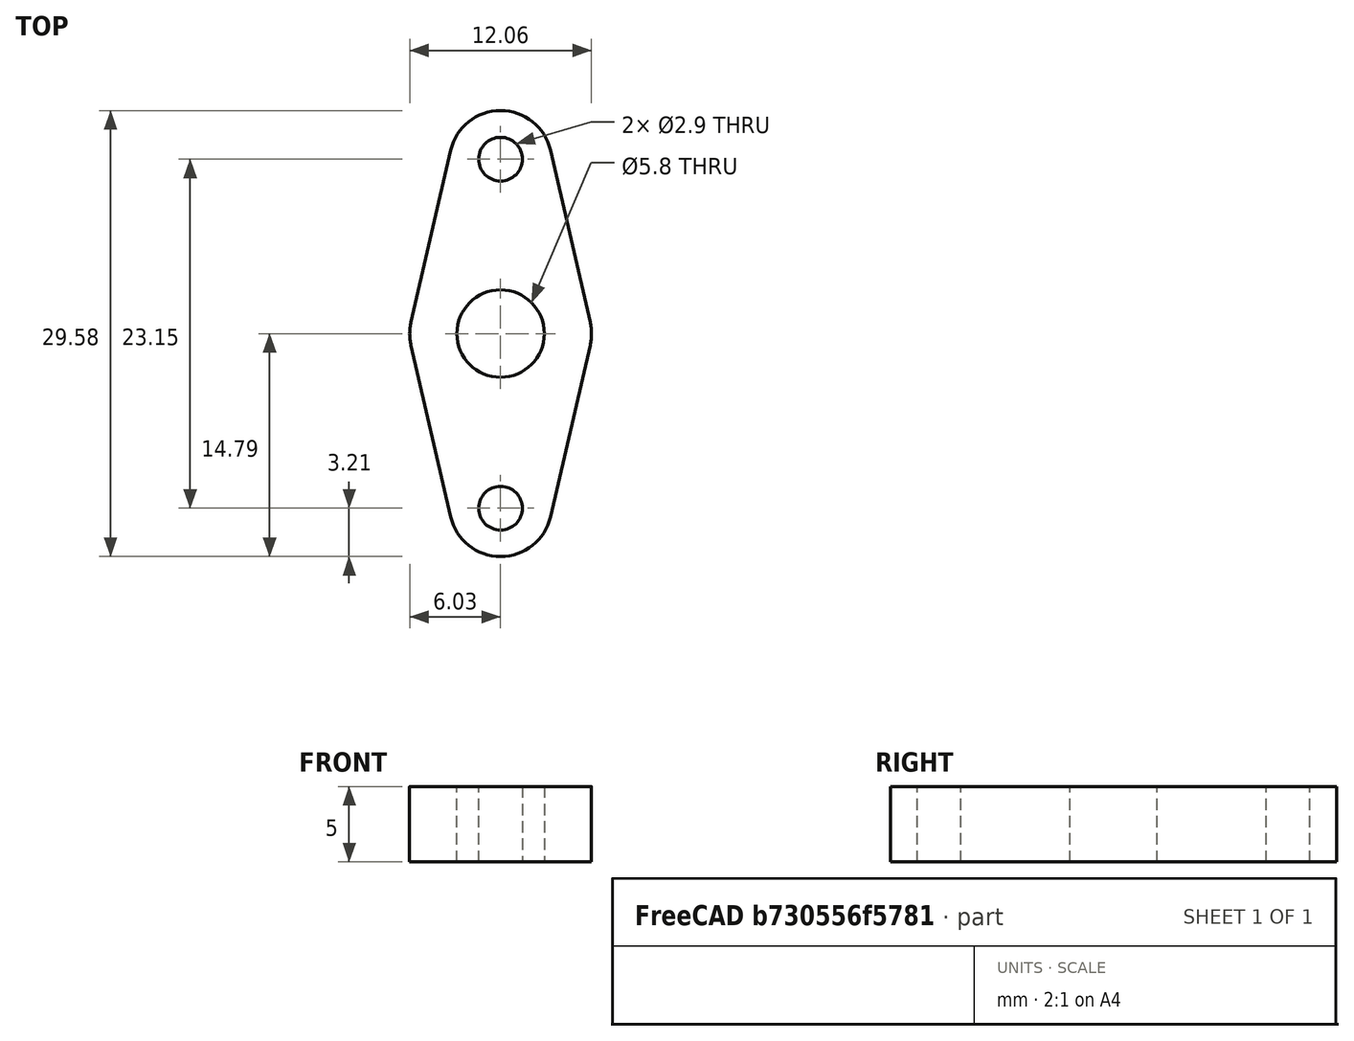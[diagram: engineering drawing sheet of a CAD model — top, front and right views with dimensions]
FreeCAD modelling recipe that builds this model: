
FCSTD DOCUMENT  (FreeCAD 0.21R33771 (Git))
Label: lens_holder_extension
License: All rights reserved
LicenseURL: http://en.wikipedia.org/wiki/All_rights_reserved
objects: Sketcher::SketchObject×2, Mesh::Feature×1, PartDesign::Pad×1, PartDesign::Fillet×1, PartDesign::Pocket×1, PartDesign::Body×1
note: 9 computed .brp shape members not serialized (recipe doc carries the construction recipe); baked Part::Feature solids carry a one-line shape summary decoded from their .brp

FEATURE [Mesh::Feature] EspressoScope_xiao_lensholder_small
  Placement = pos=(-17.04,75.5,10) rot=(0,0,1;0.763582rad)
FEATURE [Sketcher::SketchObject] Sketch
  FullyConstrained = false
  MapMode = 5
  Support = -> [XY_Plane]
  sketch-geometry (4):
    g0: LineSegment StartX=-6.12 StartY=0 StartZ=0 EndX=0 EndY=26.5 EndZ=0
    g1: LineSegment StartX=0 StartY=26.5 StartZ=0 EndX=6.11988 EndY=0 EndZ=0
    g2: LineSegment StartX=6.11988 StartY=0 StartZ=0 EndX=0 EndY=-26.5 EndZ=0
    g3: LineSegment StartX=0 StartY=-26.5 StartZ=0 EndX=-6.12 EndY=0 EndZ=0
  constraints (8):
    c: PointOnObject(g0,g-1)
    c: PointOnObject(g0,g-2)
    c: Coincident(g0,g1)
    c: PointOnObject(g1,g-1)
    c: Coincident(g1,g2)
    c: PointOnObject(g2,g-2)
    c: Coincident(g2,g3)
    c: Coincident(g3,g0)
FEATURE [PartDesign::Pad] Pad
  Direction = (0,0,1)
  Length = 5
  Length2 = 10
  Profile = -> Sketch
  ReferenceAxis = -> Sketch [N_Axis]
  Type = 0
FEATURE [PartDesign::Fillet] Fillet
  Base = -> Pad [Edge2,Edge8,Edge5,Edge1]
  BaseFeature = -> Pad
  Radius = 3.4
  SupportTransform = false
  UseAllEdges = false
FEATURE [Sketcher::SketchObject] Sketch001
  FullyConstrained = false
  MapMode = 5
  Placement = pos=(0,0,5) rot=(0,0,1;0rad)
  Support = -> [Fillet]
  sketch-geometry (3):
    g0: Circle CenterX=0 CenterY=11.57 CenterZ=0 NormalX=0 NormalY=0 NormalZ=1 AngleXU=0 Radius=1.45
    g1: Circle CenterX=0 CenterY=-11.58 CenterZ=0 NormalX=0 NormalY=0 NormalZ=1 AngleXU=0 Radius=1.45
    g2: Circle CenterX=0 CenterY=0 CenterZ=0 NormalX=0 NormalY=0 NormalZ=1 AngleXU=0 Radius=2.9
  constraints (6):
    c: PointOnObject(g0,g-2)
    c: Radius(g0) = 1.45
    c: PointOnObject(g1,g-2)
    c: Radius(g1) = 1.45
    c: Coincident(g2,g-1)
    c: Radius(g2) = 2.9
FEATURE [PartDesign::Pocket] Pocket
  BaseFeature = -> Fillet
  Direction = (0,0,-1)
  Length = 5
  Length2 = 5
  Profile = -> Sketch001
  ReferenceAxis = -> Sketch001 [N_Axis]
  Type = 1
FEATURE [PartDesign::Body] Body
  Group = -> [Sketch,Pad,Fillet,Sketch001,Pocket]
  Origin = -> Origin
  Tip = -> Pocket
